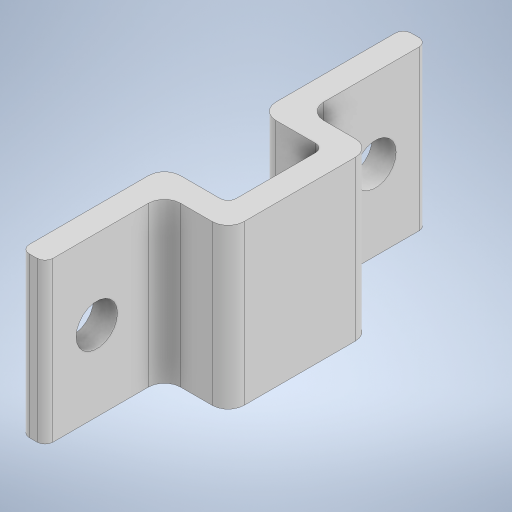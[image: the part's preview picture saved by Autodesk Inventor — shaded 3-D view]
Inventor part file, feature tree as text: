
AUTODESK INVENTOR PART (.ipt)
format: ipt  version: 2024.2 (Build 282272000, 272)  size: 267,264 bytes
history: native  units: mm
features: extrude x2, fillet x2, sketch x2, projected_geometry x2, other x1
ambient origin geometry x8: Origin, YZ Plane, XZ Plane, XY Plane, X Axis, Y Axis, Z Axis, Center Point
bodies: Body1 (feature_tree)
feature tree (9):
  other  "Bryła1"
  extrude  "Wyciągnięcie proste1"  Depth=48.0mm
  fillet  "Zaokrąglenie1"  Radius=8.0mm
  fillet  "Zaokrąglenie2"  Radius=12.0mm
  extrude  "Wyciągnięcie proste2"  Depth=3.0mm
  sketch  "Szkic1"
  sketch  "Szkic2"
  projected_geometry  "Pętla rzutowana1"
  projected_geometry  "Pętla rzutowana2"
